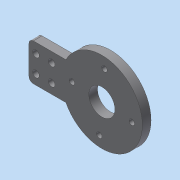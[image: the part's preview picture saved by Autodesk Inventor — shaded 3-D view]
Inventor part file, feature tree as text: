
AUTODESK INVENTOR PART (.ipt)
format: ipt  version: 2017 (Build 210142000, 142)  size: 138,752 bytes
history: native  units: in
note: dims shown in document units (in); Inventor stores cm internally (conversion verified against a paired STEP export)
features: other x8, extrude x2
ambient origin geometry x8: Origin, YZ Plane, XZ Plane, XY Plane, X Axis, Y Axis, Z Axis, Center Point
bodies: Solid1 (feature_tree)
feature tree (10):
  extrude  "plate"  Depth=2.3228in
  extrude  "motor hole"  Depth=0.125in
  other  "platethread1"
  other  "platethread2"
  other  "platethread3"
  other  "platethread4"
  other  "motorthread1"
  other  "motorthread2"
  other  "motorthread3"
  other  "motorthread4"
